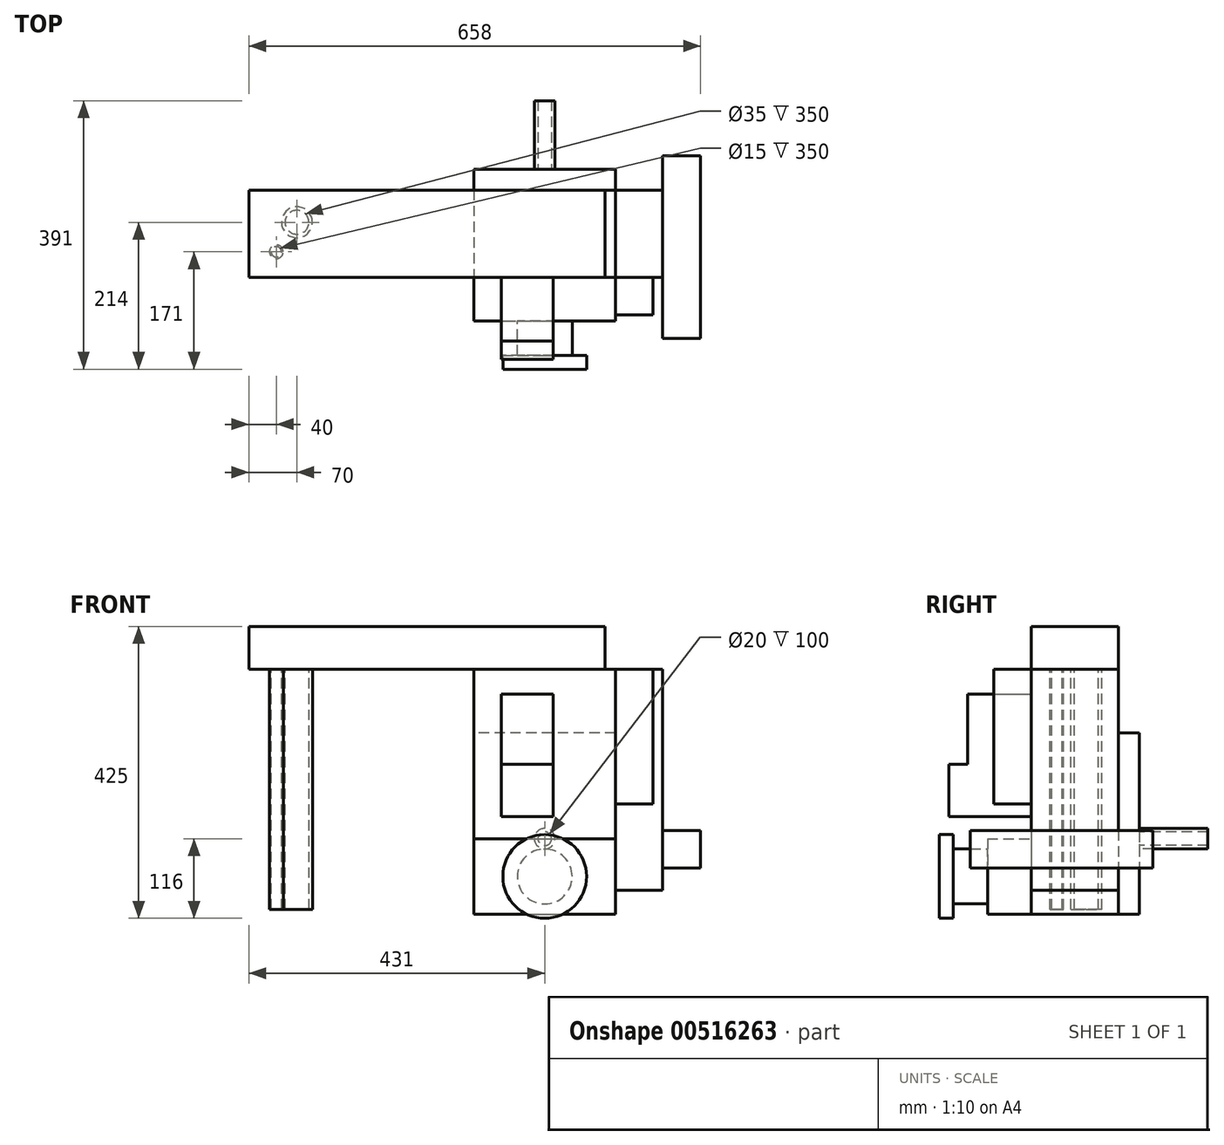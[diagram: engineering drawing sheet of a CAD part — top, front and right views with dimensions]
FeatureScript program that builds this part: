
annotation { "Feature Type Name" : "Feature", "Feature Type Description" : "" }
export const myFeature = defineFeature(function(context is Context, id is Id, definition is map)
    precondition{}
    {
        {
            var Q0;
            Q0=qCreatedBy(makeId("Front.planeOp"),FACE);
            var sketch = newSketch(context, id + "F0", { "sketchPlane" : qUnion([Q0])});
            skLineSegment(sketch, "E0.bottom", {"start": v(-206, 357) * mm, "end": v(0, 357) * mm});
            skLineSegment(sketch, "E0.top", {"start": v(-206, 0) * mm, "end": v(0, 0) * mm});
            skLineSegment(sketch, "E0.left", {"start": v(-206, 357) * mm, "end": v(-206, 0) * mm});
            skLineSegment(sketch, "E0.right", {"start": v(0, 357) * mm, "end": v(0, 0) * mm});
            skSolve(sketch);
        }
        {
            var Q0;
            Q0 = qSketchRegion(id + "F0", true);
            extrude(context, id + "F1", {"entities" : qUnion([Q0]), "oppositeDirection" : true, "depth" : 127 * mm, "offsetDistance" : 25 * mm});
        }
        {
            var Q0;
            Q0=makeQuery(id+"F1.opExtrude","SWEPT_FACE",FACE,{"disambiguationData":[OSD([sQuery(id+"F0.wireOp",EDGE,"E0.bottom")])]});
            var sketch = newSketch(context, id + "F2", { "sketchPlane" : qUnion([Q0])});
            skLineSegment(sketch, "E1.bottom", {"start": v(-15, 127) * mm, "end": v(-534, 127) * mm});
            skLineSegment(sketch, "E1.top", {"start": v(-15, 0) * mm, "end": v(-534, 0) * mm});
            skLineSegment(sketch, "E1.left", {"start": v(-15, 127) * mm, "end": v(-15, 0) * mm});
            skLineSegment(sketch, "E1.right", {"start": v(-534, 127) * mm, "end": v(-534, 0) * mm});
            skSolve(sketch);
        }
        {
            var Q0;
            Q0 = qSketchRegion(id + "F2", true);
            extrude(context, id + "F3", {"entities" : qUnion([Q0]), "depth" : 62 * mm, "offsetDistance" : 25 * mm});
        }
        {
            var Q0;
            Q0=makeQuery(id+"F1.opExtrude","SWEPT_FACE",FACE,{"disambiguationData":[OSD([sQuery(id+"F0.wireOp",EDGE,"E0.right")])]});
            var sketch = newSketch(context, id + "F4", { "sketchPlane" : qUnion([Q0])});
            skLineSegment(sketch, "E2.bottom", {"start": v(0, 357) * mm, "end": v(127, 357) * mm});
            skLineSegment(sketch, "E2.top", {"start": v(0, 35) * mm, "end": v(127, 35) * mm});
            skLineSegment(sketch, "E2.left", {"start": v(0, 357) * mm, "end": v(0, 35) * mm});
            skLineSegment(sketch, "E2.right", {"start": v(127, 357) * mm, "end": v(127, 35) * mm});
            skSolve(sketch);
        }
        {
            var Q0;
            Q0 = qSketchRegion(id + "F4", true);
            extrude(context, id + "F5", {"entities" : qUnion([Q0]), "depth" : 69 * mm, "offsetDistance" : 25 * mm});
        }
        {
            var Q0;
            Q0=makeQuery(id+"F5.opExtrude","SWEPT_FACE",FACE,{"disambiguationData":[OSD([sQuery(id+"F4.wireOp",EDGE,"E2.left")])]});
            var sketch = newSketch(context, id + "F6", { "sketchPlane" : qUnion([Q0])});
            skLineSegment(sketch, "E3.bottom", {"start": v(0, 357) * mm, "end": v(55, 357) * mm});
            skLineSegment(sketch, "E3.top", {"start": v(0, 160.69) * mm, "end": v(55, 160.69) * mm});
            skLineSegment(sketch, "E3.left", {"start": v(0, 357) * mm, "end": v(0, 160.69) * mm});
            skLineSegment(sketch, "E3.right", {"start": v(55, 357) * mm, "end": v(55, 160.69) * mm});
            skSolve(sketch);
        }
        {
            var Q0;
            Q0 = qSketchRegion(id + "F6", true);
            extrude(context, id + "F7", {"entities" : qUnion([Q0]), "depth" : 55 * mm, "offsetDistance" : 25 * mm});
        }
        {
            var Q0;
            Q0=makeQuery(id+"F5.opExtrude","CAP_FACE",FACE,{"disambiguationData":[OSD([sQuery(id+"F4.wireOp",EDGE,"E2.bottom"),sQuery(id+"F4.wireOp",EDGE,"E2.top"),sQuery(id+"F4.wireOp",EDGE,"E2.left"),sQuery(id+"F4.wireOp",EDGE,"E2.right")])],"isStart":false});
            var sketch = newSketch(context, id + "F8", { "sketchPlane" : qUnion([Q0])});
            skLineSegment(sketch, "E4.bottom", {"start": v(-89, 122) * mm, "end": v(177, 122) * mm});
            skLineSegment(sketch, "E4.top", {"start": v(-89, 67) * mm, "end": v(177, 67) * mm});
            skLineSegment(sketch, "E4.left", {"start": v(-89, 122) * mm, "end": v(-89, 67) * mm});
            skLineSegment(sketch, "E4.right", {"start": v(177, 122) * mm, "end": v(177, 67) * mm});
            skSolve(sketch);
        }
        {
            var Q0;
            Q0 = qSketchRegion(id + "F8", true);
            extrude(context, id + "F9", {"entities" : qUnion([Q0]), "depth" : 55 * mm, "offsetDistance" : 25 * mm});
        }
        {
            var Q0;
            Q0=makeQuery(id+"F1.opExtrude","CAP_FACE",FACE,{"disambiguationData":[OSD([sQuery(id+"F0.wireOp",EDGE,"E0.bottom"),sQuery(id+"F0.wireOp",EDGE,"E0.top"),sQuery(id+"F0.wireOp",EDGE,"E0.left"),sQuery(id+"F0.wireOp",EDGE,"E0.right")])],"isStart":true});
            var sketch = newSketch(context, id + "F10", { "sketchPlane" : qUnion([Q0])});
            skLineSegment(sketch, "E5.bottom", {"start": v(-166.5, 320.5) * mm, "end": v(-90.5, 320.5) * mm});
            skLineSegment(sketch, "E5.top", {"start": v(-166.5, 142.5) * mm, "end": v(-90.5, 142.5) * mm});
            skLineSegment(sketch, "E5.left", {"start": v(-166.5, 320.5) * mm, "end": v(-166.5, 142.5) * mm});
            skLineSegment(sketch, "E5.right", {"start": v(-90.5, 320.5) * mm, "end": v(-90.5, 142.5) * mm});
            skSolve(sketch);
        }
        {
            var Q0;
            Q0 = qSketchRegion(id + "F10", true);
            extrude(context, id + "F11", {"entities" : qUnion([Q0]), "depth" : 120 * mm, "offsetDistance" : 25 * mm});
        }
        {
            var Q0;
            Q0=makeQuery(id+"F11.opExtrude","CAP_FACE",FACE,{"disambiguationData":[OSD([sQuery(id+"F10.wireOp",EDGE,"E5.bottom"),sQuery(id+"F10.wireOp",EDGE,"E5.top"),sQuery(id+"F10.wireOp",EDGE,"E5.left"),sQuery(id+"F10.wireOp",EDGE,"E5.right")])],"isStart":false});
            var sketch = newSketch(context, id + "F12", { "sketchPlane" : qUnion([Q0])});
            skLineSegment(sketch, "E6.bottom", {"start": v(-171.5, 325.5) * mm, "end": v(-85.5, 325.5) * mm});
            skLineSegment(sketch, "E6.top", {"start": v(-171.5, 218.5) * mm, "end": v(-85.5, 218.5) * mm});
            skLineSegment(sketch, "E6.left", {"start": v(-171.5, 325.5) * mm, "end": v(-171.5, 218.5) * mm});
            skLineSegment(sketch, "E6.right", {"start": v(-85.5, 325.5) * mm, "end": v(-85.5, 218.5) * mm});
            skSolve(sketch);
        }
        {
            var Q0;
            Q0 = qSketchRegion(id + "F12", true);
            extrude(context, id + "F13", {"entities" : qUnion([Q0]), "operationType" : NewBodyOperationType.REMOVE, "oppositeDirection" : true, "depth" : 27 * mm, "offsetDistance" : 25 * mm});
        }
        {
            var Q0;
            Q0=makeQuery(id+"F1.opExtrude","CAP_FACE",FACE,{"disambiguationData":[OSD([sQuery(id+"F0.wireOp",EDGE,"E0.bottom"),sQuery(id+"F0.wireOp",EDGE,"E0.top"),sQuery(id+"F0.wireOp",EDGE,"E0.left"),sQuery(id+"F0.wireOp",EDGE,"E0.right")])],"isStart":true});
            var sketch = newSketch(context, id + "F14", { "sketchPlane" : qUnion([Q0])});
            skLineSegment(sketch, "E7.bottom", {"start": v(-206, 110) * mm, "end": v(0, 110) * mm});
            skLineSegment(sketch, "E7.top", {"start": v(-206, 0) * mm, "end": v(0, 0) * mm});
            skLineSegment(sketch, "E7.left", {"start": v(-206, 110) * mm, "end": v(-206, 0) * mm});
            skLineSegment(sketch, "E7.right", {"start": v(0, 110) * mm, "end": v(0, 0) * mm});
            skSolve(sketch);
        }
        {
            var Q0;
            Q0 = qSketchRegion(id + "F14", true);
            extrude(context, id + "F15", {"entities" : qUnion([Q0]), "depth" : 64 * mm, "offsetDistance" : 25 * mm});
        }
        {
            var Q0;
            Q0=makeQuery(id+"F15.opExtrude","CAP_FACE",FACE,{"disambiguationData":[OSD([sQuery(id+"F14.wireOp",EDGE,"E7.bottom"),sQuery(id+"F14.wireOp",EDGE,"E7.top"),sQuery(id+"F14.wireOp",EDGE,"E7.left"),sQuery(id+"F14.wireOp",EDGE,"E7.right")])],"isStart":false});
            var sketch = newSketch(context, id + "F16", { "sketchPlane" : qUnion([Q0])});
            skCircle(sketch, "E8", {"center": v(-103, 55) * mm, "radius": 40 * mm});
            skPoint(sketch, "E8.centerSnap0", {"position": v(-103, 110) * mm});
            skPoint(sketch, "E8.centerSnap1", {"position": v(-206, 55) * mm});
            skSolve(sketch);
        }
        {
            var Q0;
            Q0 = qSketchRegion(id + "F16", true);
            extrude(context, id + "F17", {"entities" : qUnion([Q0]), "operationType" : NewBodyOperationType.ADD, "depth" : 50 * mm, "offsetDistance" : 25 * mm});
        }
        {
            var Q0;
            Q0=makeQuery(id+"F17.opExtrude","CAP_FACE",FACE,{"disambiguationData":[OSD([sQuery(id+"F16.wireOp",EDGE,"E8")])],"isStart":false});
            var sketch = newSketch(context, id + "F18", { "sketchPlane" : qUnion([Q0])});
            skCircle(sketch, "E9", {"center": v(-103, 55) * mm, "radius": 61 * mm});
            skSolve(sketch);
        }
        {
            var Q0;
            Q0 = qSketchRegion(id + "F18", true);
            extrude(context, id + "F19", {"entities" : qUnion([Q0]), "operationType" : NewBodyOperationType.ADD, "depth" : 20 * mm, "offsetDistance" : 25 * mm});
        }
        {
            var Q0;
            Q0=makeQuery(id+"F1.opExtrude","CAP_FACE",FACE,{"disambiguationData":[OSD([sQuery(id+"F0.wireOp",EDGE,"E0.bottom"),sQuery(id+"F0.wireOp",EDGE,"E0.top"),sQuery(id+"F0.wireOp",EDGE,"E0.left"),sQuery(id+"F0.wireOp",EDGE,"E0.right")])],"isStart":false});
            var sketch = newSketch(context, id + "F20", { "sketchPlane" : qUnion([Q0])});
            skLineSegment(sketch, "E10.bottom", {"start": v(0, 264) * mm, "end": v(206, 264) * mm});
            skLineSegment(sketch, "E10.top", {"start": v(0, 0) * mm, "end": v(206, 0) * mm});
            skLineSegment(sketch, "E10.left", {"start": v(0, 264) * mm, "end": v(0, 0) * mm});
            skLineSegment(sketch, "E10.right", {"start": v(206, 264) * mm, "end": v(206, 0) * mm});
            skSolve(sketch);
        }
        {
            var Q0;
            Q0 = qSketchRegion(id + "F20", true);
            extrude(context, id + "F21", {"entities" : qUnion([Q0]), "depth" : 30 * mm, "offsetDistance" : 25 * mm});
        }
        {
            var Q0;
            Q0=makeQuery(id+"F21.opExtrude","CAP_FACE",FACE,{"disambiguationData":[OSD([sQuery(id+"F20.wireOp",EDGE,"E10.bottom"),sQuery(id+"F20.wireOp",EDGE,"E10.top"),sQuery(id+"F20.wireOp",EDGE,"E10.left"),sQuery(id+"F20.wireOp",EDGE,"E10.right")])],"isStart":false});
            var sketch = newSketch(context, id + "F22", { "sketchPlane" : qUnion([Q0])});
            skCircle(sketch, "E11", {"center": v(103, 110) * mm, "radius": 10 * mm});
            skCircle(sketch, "E12", {"center": v(103, 110) * mm, "radius": 15 * mm});
            skSolve(sketch);
        }
        {
            var Q0;
            Q0 = qSketchRegion(id + "F22", true);
            extrude(context, id + "F23", {"entities" : qUnion([Q0]), "operationType" : NewBodyOperationType.ADD, "depth" : 100 * mm, "offsetDistance" : 25 * mm});
        }
        {
            var Q0;
            Q0=makeQuery(id+"F3.opExtrude","CAP_FACE",FACE,{"disambiguationData":[OSD([sQuery(id+"F2.wireOp",EDGE,"E1.bottom"),sQuery(id+"F2.wireOp",EDGE,"E1.top"),sQuery(id+"F2.wireOp",EDGE,"E1.left"),sQuery(id+"F2.wireOp",EDGE,"E1.right")])],"isStart":true});
            var sketch = newSketch(context, id + "F24", { "sketchPlane" : qUnion([Q0])});
            skCircle(sketch, "E13", {"center": v(-464, -80) * mm, "radius": 22.5 * mm});
            skCircle(sketch, "E14", {"center": v(-464, -80) * mm, "radius": 17.5 * mm});
            skCircle(sketch, "E15", {"center": v(-494, -37) * mm, "radius": 7.5 * mm});
            skCircle(sketch, "E16", {"center": v(-494, -37) * mm, "radius": 10 * mm});
            skSolve(sketch);
        }
        {
            var Q0;
            Q0 = qSketchRegion(id + "F24", true);
            extrude(context, id + "F25", {"entities" : qUnion([Q0]), "depth" : 350 * mm, "offsetDistance" : 25 * mm});
        }
    });
